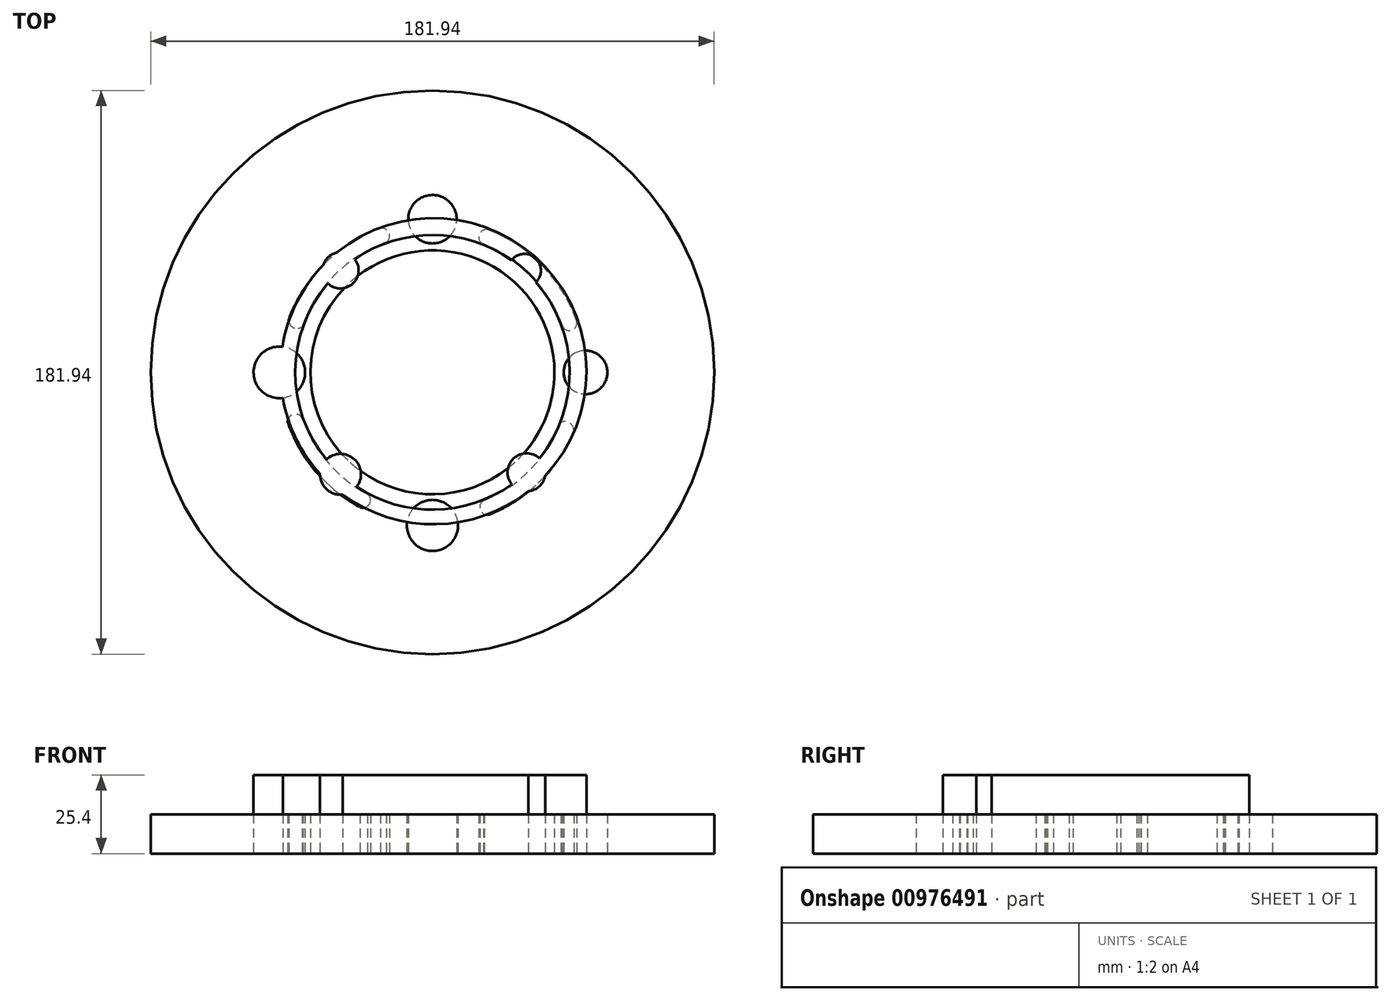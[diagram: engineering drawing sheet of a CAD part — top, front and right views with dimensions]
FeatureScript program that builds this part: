
annotation { "Feature Type Name" : "Feature", "Feature Type Description" : "" }
export const myFeature = defineFeature(function(context is Context, id is Id, definition is map)
    precondition{}
    {
        {
            var Q0;
            Q0=qCreatedBy(makeId("Top.planeOp"),FACE);
            var sketch = newSketch(context, id + "F0", { "sketchPlane" : qUnion([Q0])});
            skCircle(sketch, "E0", {"center": v(0, 0) * mm, "radius": 90.97 * mm});
            skArc(sketch, "E1", {"start": v(-46.7, -16.24) * mm, "mid": v(-37.61, -32.08) * mm, "end": v(-23.4, -43.55) * mm});
            skCircle(sketch, "E2", {"center": v(0, 49.44) * mm, "radius": 7.83 * mm});
            skCircle(sketch, "E3", {"center": v(49.44, 0) * mm, "radius": 7.05 * mm});
            skCircle(sketch, "E4", {"center": v(0, -49.44) * mm, "radius": 8.26 * mm});
            skCircle(sketch, "E5", {"center": v(-49.44, 0) * mm, "radius": 8.33 * mm});
            skArc(sketch, "E6", {"start": v(-41.82, -15.38) * mm, "mid": v(-33.6, -29.27) * mm, "end": v(-20.96, -39.32) * mm});
            skArc(sketch, "E7", {"start": v(-41.82, -15.38) * mm, "mid": v(-44.66, -13.49) * mm, "end": v(-46.7, -16.24) * mm});
            skArc(sketch, "E8", {"start": v(-23.4, -43.55) * mm, "mid": v(-20.33, -42.5) * mm, "end": v(-20.96, -39.32) * mm});
            skArc(sketch, "E9", {"start": v(16.7, -41.31) * mm, "mid": v(15.5, -44.51) * mm, "end": v(18.67, -45.77) * mm});
            skArc(sketch, "E10", {"start": v(45.65, -18.99) * mm, "mid": v(44.4, -16.4) * mm, "end": v(41.56, -16.08) * mm});
            skArc(sketch, "E11", {"start": v(18.31, 45.92) * mm, "mid": v(15.14, 44.58) * mm, "end": v(16.47, 41.4) * mm});
            skArc(sketch, "E12", {"start": v(41.98, 14.93) * mm, "mid": v(45.13, 13.68) * mm, "end": v(46.5, 16.78) * mm});
            skArc(sketch, "E13", {"start": v(-46.44, 16.94) * mm, "mid": v(-44.93, 14.46) * mm, "end": v(-42.04, 14.76) * mm});
            skArc(sketch, "E14", {"start": v(-14.85, 42.01) * mm, "mid": v(-14.06, 45.03) * mm, "end": v(-16.81, 46.5) * mm});
            skArc(sketch, "E15.trimOffspring", {"start": v(-14.85, 42.01) * mm, "mid": v(-31.54, 31.47) * mm, "end": v(-42.04, 14.76) * mm});
            skArc(sketch, "E16.trimOffspring", {"start": v(-16.81, 46.5) * mm, "mid": v(-34.9, 35) * mm, "end": v(-46.44, 16.94) * mm});
            skArc(sketch, "E17.trimOffspring", {"start": v(46.5, 16.78) * mm, "mid": v(35.53, 34.37) * mm, "end": v(18.31, 45.92) * mm});
            skArc(sketch, "E18.trimOffspring", {"start": v(41.98, 14.93) * mm, "mid": v(32.09, 30.92) * mm, "end": v(16.47, 41.4) * mm});
            skArc(sketch, "E19.trimOffspring", {"start": v(16.7, -41.31) * mm, "mid": v(31.74, -31.27) * mm, "end": v(41.56, -16.08) * mm});
            skArc(sketch, "E20.trimOffspring", {"start": v(18.63, -45.8) * mm, "mid": v(34.82, -35.1) * mm, "end": v(45.65, -18.99) * mm});
            skSolve(sketch);
        }
        {
            var Q0;
            Q0=makeQuery(id+"F0.imprint","IMPRINT",FACE,{"disambiguationData":[TD([[makeQuery(id+"F0.imprint","IMPRINT",EDGE,{"derivedFrom":sQuery(id+"F0.wireOp",EDGE,"E0")}),1.0]])]});
            var sketch = newSketch(context, id + "F1", { "sketchPlane" : qUnion([Q0])});
            skArc(sketch, "E21", {"start": v(-33.75, 28.73) * mm, "mid": v(-44.32, 0.38) * mm, "end": v(-34.24, -28.15) * mm});
            skCircle(sketch, "E22", {"center": v(-29.68, 32.92) * mm, "radius": 5.84 * mm});
            skCircle(sketch, "E23", {"center": v(29.68, 32.92) * mm, "radius": 5.33 * mm});
            skCircle(sketch, "E24", {"center": v(30.38, -32.28) * mm, "radius": 6.13 * mm});
            skCircle(sketch, "E25", {"center": v(-29.68, -32.92) * mm, "radius": 6.6 * mm});
            skLineSegment(sketch, "E26.trimOffspring", {"start": v(0, 0) * mm, "end": v(0.32, 0.35) * mm});
            skArc(sketch, "E27", {"start": v(-35.26, 34.65) * mm, "mid": v(-49.1, 1.1) * mm, "end": v(-36.28, -32.84) * mm});
            skArc(sketch, "E28.trimOffspring", {"start": v(-24.47, -36.96) * mm, "mid": v(0.7, -44.32) * mm, "end": v(25.64, -36.16) * mm});
            skArc(sketch, "E29.trimOffspring", {"start": v(-28.93, -39.47) * mm, "mid": v(1.23, -49.05) * mm, "end": v(31.01, -38.37) * mm});
            skArc(sketch, "E30.trimOffspring", {"start": v(34.54, -27.78) * mm, "mid": v(44.32, 0.87) * mm, "end": v(33.42, 29.11) * mm});
            skArc(sketch, "E31.trimOffspring", {"start": v(36.4, -33.4) * mm, "mid": v(36.4, 34.1) * mm, "end": v(-30.95, 38.61) * mm});
            skArc(sketch, "E32.trimOffspring", {"start": v(25.52, 36.24) * mm, "mid": v(0.25, 44.32) * mm, "end": v(-25.1, 36.53) * mm});
            skSolve(sketch);
        }
        {
            var Q0;
            Q0 = qSketchRegion(id + "F1", true);
            var Q1;
            {var subQ0=sQuery(id+"F1.wireOp",EDGE,"E27");Q1=makeQuery(id+"F1.imprint","IMPRINT",FACE,{"disambiguationData":[TD([[makeQuery(id+"F1.imprint","IMPRINT",EDGE,{"derivedFrom":subQ0}),-1.0]])]});}
            extrude(context, id + "F2", {"entities" : qUnion([Q0, Q1]), "depth" : 25.4 * mm, "offsetDistance" : 25.4 * mm});
        }
        {
            var Q0;
            Q0=makeQuery(id+"F0.imprint","IMPRINT",FACE,{"disambiguationData":[TD([[makeQuery(id+"F0.imprint","IMPRINT",EDGE,{"derivedFrom":sQuery(id+"F0.wireOp",EDGE,"E0")}),1.0]])]});
            var sketch = newSketch(context, id + "F3", { "sketchPlane" : qUnion([Q0])});
            skCircle(sketch, "E33", {"center": v(0, 0) * mm, "radius": 39.4 * mm});
            skSolve(sketch);
        }
        {
            var Q0;
            Q0=makeQuery(id+"F3.imprint","IMPRINT",FACE,{"disambiguationData":[TD([[makeQuery(id+"F3.imprint","IMPRINT",EDGE,{"derivedFrom":sQuery(id+"F3.wireOp",EDGE,"E33")}),-1.0]])]});
            extrude(context, id + "F4", {"entities" : qUnion([Q0]), "depth" : 12.7 * mm, "offsetDistance" : 25.4 * mm});
        }
    });
